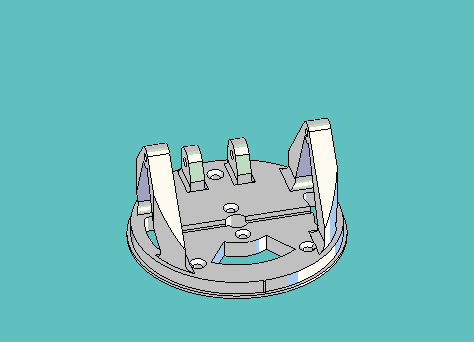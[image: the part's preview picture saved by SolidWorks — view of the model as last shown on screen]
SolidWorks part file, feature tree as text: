
SOLIDWORKS PART (.sldprt)
format: sldprt  version: not decoded by parser v0  size: 1,510,400 bytes
history: native  units: mm
features: sketch x19, cut_extrude x11, extrude x7, plane x7, chamfer x2, fillet x2, material x1 (+11 scaffold rows collapsed)
feature tree (60):
  scaffold x11  (default folders/planes/origin — collapsed)
  material  "Material <not specified>"
  sketch  "Sketch1"  dims[c1.D1=50.8mm c1.D7=3.175mm c2.D1=88.9mm c2.D2=~93.32036mm c3.D2=45.0deg c3.D3=~94.913632mm c4.D3=45.0deg c4.D4=6.35mm c4.D5=6.35mm c4.D6=31.75mm]
  extrude  "Extrude1"  Depth=7.14375mm
  sketch  "Sketch29"  dims[D1=1.5875mm]
  extrude  "Extrude10"  Depth=1.27mm
  sketch  "Sketch3"  dims[c1.D1=3.4544mm c1.D2=3.4544mm c1.D3=9.525mm c2.D2=3.4544mm c2.D4=3.4544mm c2.D1=19.558mm c2.D5=~22.869813mm c3.D5=30.0deg]
  cut_extrude  "Cut-Extrude2"  [1 undecoded]
  chamfer  "Chamfer2"  Distance=1.5875mm Angle=45deg
  sketch  "Sketch5"  dims[c1.D3=19.05mm c1.D4=25.4mm c1.D1=20.6375mm c1.D2=20.6375mm c1.D5=~49.79749mm c2.D5=30.0deg c2.D6=11.1125mm c2.D1=17.145mm c2.D2=17.145mm c3.D1=~82.457251mm c4.D1=90.0deg c4.D2=9.525mm c4.D3=9.525mm]
  sketch  "Sketch6"  dims[D1=9.525mm]
  extrude  "Axis2"  [1 undecoded]
  plane  "Plane1"
  sketch  "Sketch30"  dims[c1.D1=0.508mm c1.D2=1.143mm c1.D3=1.016mm c1.D4=1.016mm c1.D5=0.381mm c1.D6=0.381mm c1.D7=~0.963455mm c2.D7=20.0deg c2.D8=~0.965449mm c3.D8=20.0deg]
  extrude  "Extrude11"  [1 undecoded]
  sketch  "Sketch25"  dims[D1=4.7625mm]
  cut_extrude  "Cut-Extrude18"  Depth=34.925mm
  plane  "Plane2"
  plane  "Plane3"  Offset=50.8mm
  sketch  "Sketch11"  dims[c1.D1=40.3225mm c1.D2=40.3225mm c2.D1=22.86mm c2.D2=24.384mm c2.D3=30.1625mm c2.D4=30.1625mm]
  extrude  "Extrude6"  Depth=44.45mm
  sketch  "Sketch7"  dims[D1=3.4544mm D2=4.7625mm]
  cut_extrude  "Cut-Extrude7"  [1 undecoded]
  sketch  "Sketch12"  dims[D1=6.35mm D2=6.35mm D3=6.35mm]
  cut_extrude  "Cut-Extrude9"  [1 undecoded]
  sketch  "Sketch15"  dims[c1.D4=3.175mm c1.D1=9.525mm c1.D2=9.525mm c1.D3=9.525mm c2.D1=9.525mm c2.D2=9.525mm c2.D5=25.4mm c2.D6=25.4mm]
  cut_extrude  "Cut-Extrude12"  [1 undecoded]
  fillet  "Fillet3"  Radius=3.175mm
  plane  "Plane4"  Offset=7.14375mm
  plane  "Plane5"  Offset=7.14375mm
  sketch  "Sketch17"  dims[c1.D4=~3.96875mm c1.D1=28.575mm c1.D2=9.525mm c1.D3=6.35mm c2.D1=34.925mm c2.D5=~9.745748mm c2.D3=9.525mm c3.D5=6.35mm c3.D6=6.35mm c3.D2=~11.90625mm c4.D5=~8.73125mm c4.D7=4.7625mm]
  extrude  "Extrude8"  Depth=5.969mm
  sketch  "Sketch18"  dims[D1=0.0mm]
  extrude  "Extrude9"  Depth=5.969mm
  fillet  "Fillet5"  Radius=1.5875mm
  plane  "Plane6"  Offset=39.6875mm
  plane  "Plane7"  Offset=39.6875mm
  sketch  "Sketch19"  dims[D1=12.7mm]
  cut_extrude  "Cut-Extrude14"  [1 undecoded]
  sketch  "Sketch20"
  cut_extrude  "Cut-Extrude15"  [1 undecoded]
  sketch  "Sketch21"  dims[D1=~2.38125mm]
  cut_extrude  "Cut-Extrude16"  [1 undecoded]
  sketch  "Sketch24"  dims[c1.D1=~3.96875mm c1.D2=~3.96875mm c1.D3=~3.96875mm c1.D5=69.85mm c1.D4=~57.085134mm c2.D4=210.0deg c2.D6=~57.085134mm c3.D6=137.0deg c3.D7=~57.085134mm c4.D7=137.0deg]
  cut_extrude  "Cut-Extrude17"  [1 undecoded]
  chamfer  "Chamfer1"  Distance=1.5875mm Angle=45deg
  sketch  "Sketch27"  dims[c1.D1=82.55mm c1.D4=6.35mm c1.D5=60.325mm c1.D2=~49.526136mm c2.D2=30.0deg c3.D2=~53.156372mm c4.D2=30.0deg c4.D3=35.56mm c4.D6=~50.104381mm c5.D6=15.0deg c5.D7=~51.861275mm c6.D7=15.0deg]
  cut_extrude  "Cut-Extrude19"  [1 undecoded]
  sketch  "Sketch28"  dims[c1.D4=19.05mm c1.D5=9.525mm c1.D7=31.75mm c1.D8=4.7625mm c1.D2=31.75mm c1.D1=~114.757699mm c2.D1=30.0deg c2.D2=19.05mm c2.D3=31.75mm c2.D4=~114.757699mm c3.D4=35.0deg c3.D6=~114.757699mm c4.D6=35.0deg c4.D2=15.875mm c4.D3=1.5875mm]
  cut_extrude  "Cut-Extrude20"  [1 undecoded]
decode coverage: 28 of 41 modeling features carry decoded parameters
note: ~ marks probable driven/reference dimensions
note: 12 parameter values undecoded
summary: no parameter record found for 12 features
note: suppression state not decoded; provenance and decode notes live in map.json
